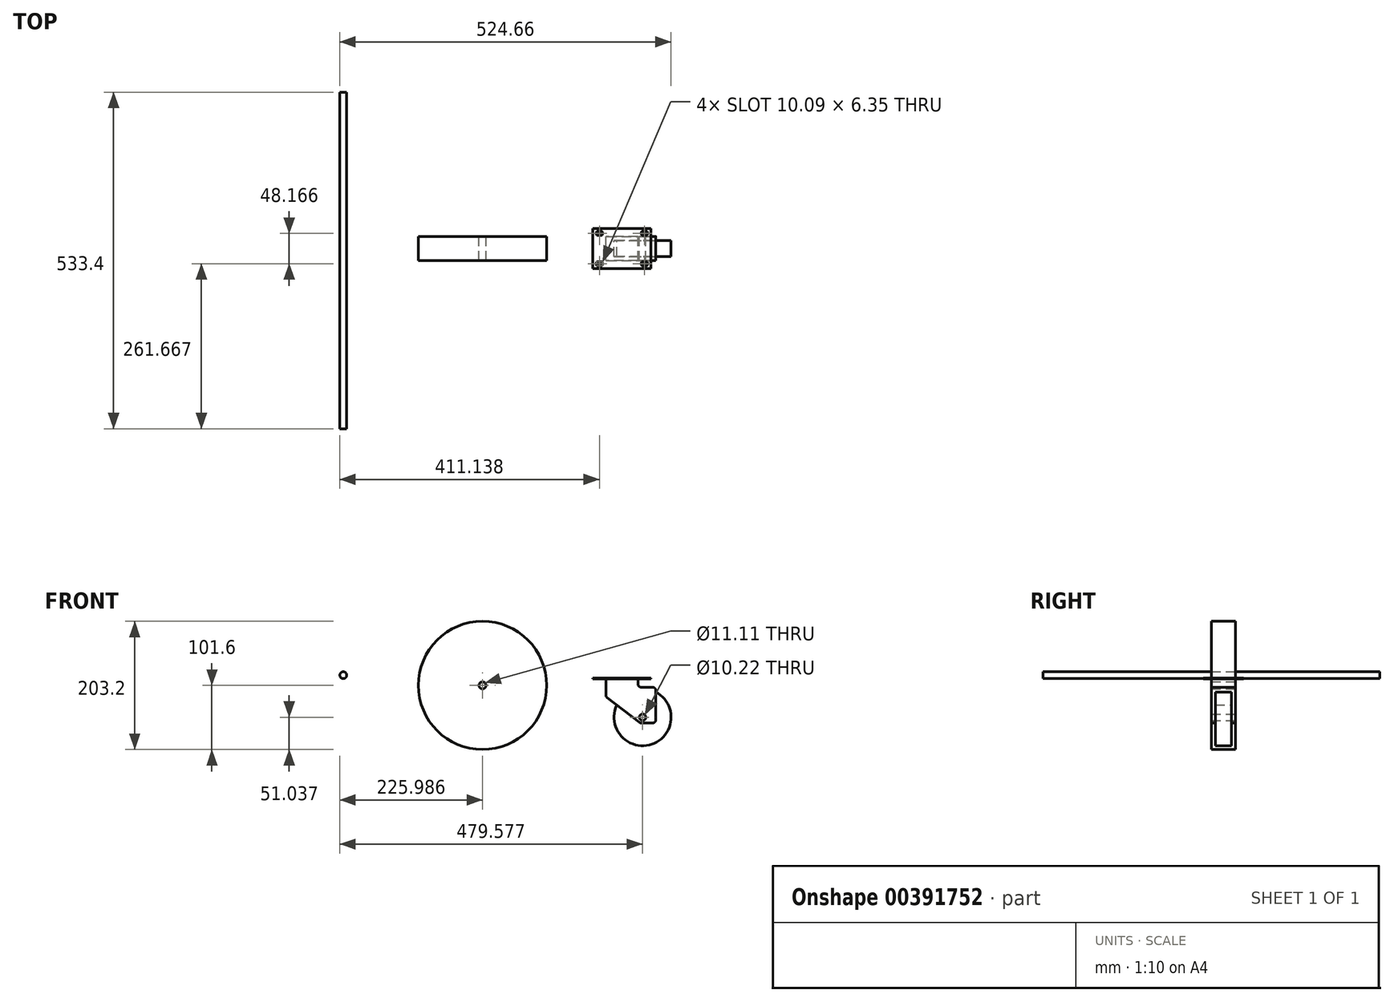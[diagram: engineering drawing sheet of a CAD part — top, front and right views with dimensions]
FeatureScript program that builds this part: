
annotation { "Feature Type Name" : "Feature", "Feature Type Description" : "" }
export const myFeature = defineFeature(function(context is Context, id is Id, definition is map)
    precondition{}
    {
        {
            var Q0;
            Q0=qCreatedBy(makeId("Front.planeOp"),FACE);
            var sketch = newSketch(context, id + "F0", { "sketchPlane" : qUnion([Q0])});
            skLineSegment(sketch, "E0.bottom", {"start": v(53.18, 10) * mm, "end": v(-38.9, 10) * mm});
            skLineSegment(sketch, "E0.top", {"start": v(53.18, 11.59) * mm, "end": v(-38.9, 11.59) * mm});
            skLineSegment(sketch, "E0.left", {"start": v(53.18, 10) * mm, "end": v(53.18, 11.59) * mm});
            skLineSegment(sketch, "E0.right", {"start": v(-38.9, 10) * mm, "end": v(-38.9, 11.59) * mm});
            skLineSegment(sketch, "E1", {"start": v(-18.26, 10) * mm, "end": v(-18.26, -18.05) * mm});
            skLineSegment(sketch, "E2", {"start": v(-18.26, -18.05) * mm, "end": v(36.1, -59.65) * mm});
            skLineSegment(sketch, "E3", {"start": v(36.1, -59.65) * mm, "end": v(60.69, -59.65) * mm});
            skLineSegment(sketch, "E4", {"start": v(60.69, -59.65) * mm, "end": v(60.69, -2.98) * mm});
            skLineSegment(sketch, "E5", {"start": v(60.69, -2.98) * mm, "end": v(32.54, -2.98) * mm});
            skLineSegment(sketch, "E6", {"start": v(32.54, -2.98) * mm, "end": v(32.54, 10) * mm});
            skCircle(sketch, "E7", {"center": v(39.87, -50.56) * mm, "radius": 45.08 * mm});
            skCircle(sketch, "E8", {"center": v(39.87, -50.56) * mm, "radius": 5.1 * mm});
            skSolve(sketch);
        }
        {
            var Q0;
            Q0=makeQuery(id+"F0.imprint","IMPRINT",FACE,{"disambiguationData":[TD([[makeQuery(id+"F0.imprint","IMPRINT",EDGE,{"derivedFrom":sQuery(id+"F0.wireOp",EDGE,"E0.top")}),1.0]])]});
            extrude(context, id + "F1", {"entities" : qUnion([Q0]), "endBound" : BoundingType.SYMMETRIC, "depth" : 63.5 * mm});
        }
        {
            var Q0;
            {var subQ0=sQuery(id+"F0.wireOp",EDGE,"E3");Q0=makeQuery(id+"F0.imprint","IMPRINT",FACE,{"disambiguationData":[TD([[makeQuery(id+"F0.imprint","IMPRINT",EDGE,{"derivedFrom":subQ0}),-1.0]])]});}
            var Q1;
            {var subQ5=sQuery(id+"F0.wireOp",EDGE,"E3");Q1=makeQuery(id+"F0.imprint","IMPRINT",FACE,{"disambiguationData":[TD([[makeQuery(id+"F0.imprint","IMPRINT",EDGE,{"derivedFrom":subQ5}),1.0]])]});}
            extrude(context, id + "F2", {"entities" : qUnion([Q0, Q1]), "endBound" : BoundingType.SYMMETRIC, "depth" : 25.4 * mm});
        }
        {
            var Q0;
            {var subQ5=sQuery(id+"F0.wireOp",EDGE,"E1");Q0=makeQuery(id+"F0.imprint","IMPRINT",FACE,{"disambiguationData":[TD([[makeQuery(id+"F0.imprint","IMPRINT",EDGE,{"derivedFrom":subQ5}),1.0]])]});}
            var Q1;
            {var subQ5=sQuery(id+"F0.wireOp",EDGE,"E3");Q1=makeQuery(id+"F0.imprint","IMPRINT",FACE,{"disambiguationData":[TD([[makeQuery(id+"F0.imprint","IMPRINT",EDGE,{"derivedFrom":subQ5}),1.0]])]});}
            extrude(context, id + "F3", {"entities" : qUnion([Q0, Q1]), "operationType" : NewBodyOperationType.ADD, "endBound" : BoundingType.SYMMETRIC, "depth" : 38.1 * mm});
        }
        {
            var Q0;
            Q0=makeQuery(id+"F3.opExtrude","SWEPT_EDGE",EDGE,{"disambiguationData":[OSD([sQuery(id+"F0.wireOp",EDGE,"E4"),sQuery(id+"F0.wireOp",EDGE,"E5")])]});
            var Q1;
            Q1=makeQuery(id+"F3.opExtrude","SWEPT_EDGE",EDGE,{"disambiguationData":[OSD([sQuery(id+"F0.wireOp",EDGE,"E3"),sQuery(id+"F0.wireOp",EDGE,"E4")])]});
            var Q2;
            Q2=makeQuery(id+"F3.opExtrude","SWEPT_EDGE",EDGE,{"disambiguationData":[OSD([sQuery(id+"F0.wireOp",EDGE,"E2"),sQuery(id+"F0.wireOp",EDGE,"E3")])]});
            var Q3;
            Q3=makeQuery(id+"F3.opExtrude","SWEPT_EDGE",EDGE,{"disambiguationData":[OSD([sQuery(id+"F0.wireOp",EDGE,"E1"),sQuery(id+"F0.wireOp",EDGE,"E2")])]});
            var Q4;
            Q4=makeQuery(id+"F3.opExtrude","SWEPT_EDGE",EDGE,{"disambiguationData":[OSD([sQuery(id+"F0.wireOp",EDGE,"E5"),sQuery(id+"F0.wireOp",EDGE,"E6")])]});
            fillet(context, id + "F4", {"entities" : qUnion([Q0, Q1, Q2, Q3, Q4]), "radius" : 5.08 * mm, "tangentPropagation" : true, "allowEdgeOverflow" : false});
        }
        {
            var Q0;
            Q0=qCreatedBy(makeId("Top.planeOp"),FACE);
            var sketch = newSketch(context, id + "F5", { "sketchPlane" : qUnion([Q0])});
            skArc(sketch, "E9", {"start": v(-24.65, 20.9) * mm, "mid": v(-23.53, 24.08) * mm, "end": v(-24.65, 27.26) * mm});
            skLineSegment(sketch, "E10.bottom", {"start": v(-32.6, 27.26) * mm, "end": v(-24.65, 27.26) * mm});
            skLineSegment(sketch, "E10.top", {"start": v(-32.6, 20.9) * mm, "end": v(-24.65, 20.9) * mm});
            skArc(sketch, "E11.MirrorCS", {"start": v(-32.5, 20.9) * mm, "mid": v(-33.61, 24.08) * mm, "end": v(-32.5, 27.26) * mm});
            skLineSegment(sketch, "E12.MirrorCS", {"start": v(46.78, 20.9) * mm, "end": v(38.85, 20.9) * mm});
            skLineSegment(sketch, "E13.MirrorCS", {"start": v(46.78, 27.26) * mm, "end": v(38.85, 27.26) * mm});
            skArc(sketch, "E14.MirrorCS", {"start": v(46.68, 20.9) * mm, "mid": v(47.8, 24.08) * mm, "end": v(46.68, 27.26) * mm});
            skArc(sketch, "E15.MirrorCS", {"start": v(38.85, 20.9) * mm, "mid": v(37.72, 24.08) * mm, "end": v(38.85, 27.26) * mm});
            skLineSegment(sketch, "E16.MirrorCS", {"start": v(-32.6, -20.9) * mm, "end": v(-24.65, -20.9) * mm});
            skLineSegment(sketch, "E17.MirrorCS", {"start": v(-32.6, -27.26) * mm, "end": v(-24.65, -27.26) * mm});
            skArc(sketch, "E18.MirrorCS", {"start": v(-32.5, -20.9) * mm, "mid": v(-33.61, -24.08) * mm, "end": v(-32.5, -27.26) * mm});
            skArc(sketch, "E19.MirrorCS", {"start": v(-24.65, -20.9) * mm, "mid": v(-23.53, -24.08) * mm, "end": v(-24.65, -27.26) * mm});
            skArc(sketch, "E20.MirrorCS", {"start": v(38.85, -20.9) * mm, "mid": v(37.72, -24.08) * mm, "end": v(38.85, -27.26) * mm});
            skLineSegment(sketch, "E21.MirrorCS", {"start": v(46.78, -20.9) * mm, "end": v(38.85, -20.9) * mm});
            skLineSegment(sketch, "E22.MirrorCS", {"start": v(46.78, -27.26) * mm, "end": v(38.85, -27.26) * mm});
            skArc(sketch, "E23.MirrorCS", {"start": v(46.68, -20.9) * mm, "mid": v(47.8, -24.08) * mm, "end": v(46.68, -27.26) * mm});
            skSolve(sketch);
        }
        {
            var Q0;
            Q0=qSketchRegion(id+"F5",true);
            extrude(context, id + "F6", {"entities" : qUnion([Q0]), "operationType" : NewBodyOperationType.REMOVE, "endBound" : BoundingType.THROUGH_ALL, "depth" : 25.4 * mm});
        }
        {
            var Q0;
            Q0=qCreatedBy(makeId("Front.planeOp"),FACE);
            var sketch = newSketch(context, id + "F7", { "sketchPlane" : qUnion([Q0])});
            skCircle(sketch, "E24", {"center": v(-213.72, 0) * mm, "radius": 101.6 * mm});
            skCircle(sketch, "E25", {"center": v(-213.72, 0) * mm, "radius": 5.56 * mm});
            skSolve(sketch);
        }
        {
            var Q0;
            Q0=makeQuery(id+"F7.imprint","IMPRINT",FACE,{"disambiguationData":[TD([[makeQuery(id+"F7.imprint","IMPRINT",EDGE,{"derivedFrom":sQuery(id+"F7.wireOp",EDGE,"E24")}),1.0]])]});
            extrude(context, id + "F8", {"entities" : qUnion([Q0]), "endBound" : BoundingType.SYMMETRIC, "depth" : 38.1 * mm});
        }
        {
            var Q0;
            Q0=makeQuery(id+"F8.opExtrude","CAP_FACE",FACE,{"disambiguationData":[OSD([sQuery(id+"F7.wireOp",EDGE,"E24"),sQuery(id+"F7.wireOp",EDGE,"E25")])],"isStart":false});
            var sketch = newSketch(context, id + "F9", { "sketchPlane" : qUnion([Q0])});
            skCircle(sketch, "E26", {"center": v(-434.25, 16.14) * mm, "radius": 5.46 * mm});
            skSolve(sketch);
        }
        {
            var Q0;
            Q0=makeQuery(id+"F9.imprint","IMPRINT",FACE,{"disambiguationData":[TD([[makeQuery(id+"F9.imprint","IMPRINT",EDGE,{"derivedFrom":sQuery(id+"F9.wireOp",EDGE,"E26")}),1.0]])]});
            extrude(context, id + "F10", {"entities" : qUnion([Q0]), "endBound" : BoundingType.SYMMETRIC, "depth" : 533.4 * mm});
        }
    });
